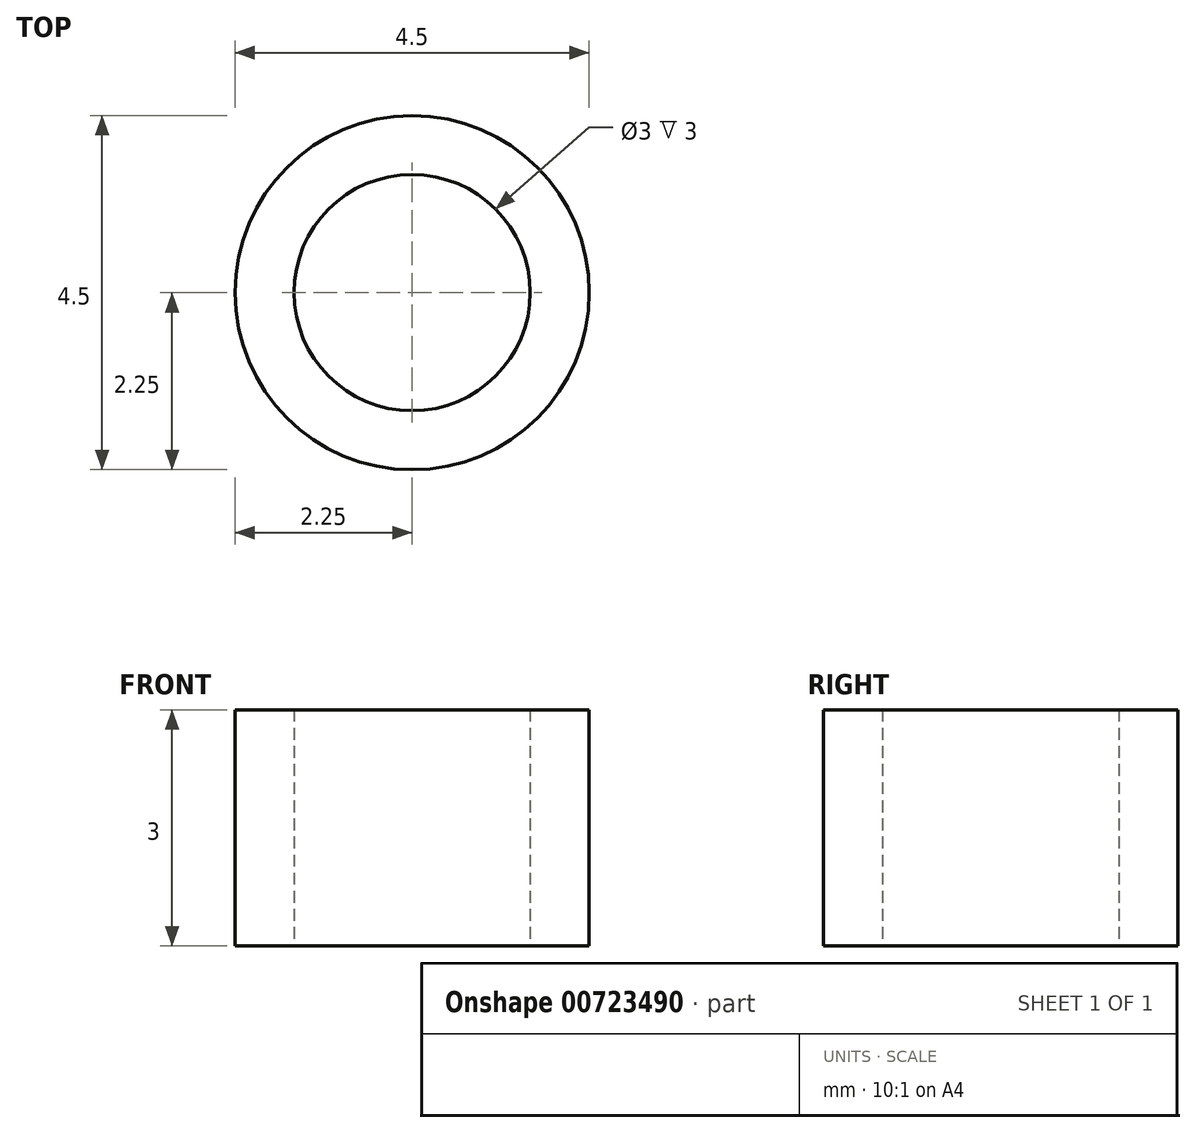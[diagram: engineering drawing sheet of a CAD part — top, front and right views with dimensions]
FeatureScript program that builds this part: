
annotation { "Feature Type Name" : "Feature", "Feature Type Description" : "" }
export const myFeature = defineFeature(function(context is Context, id is Id, definition is map)
    precondition{}
    {
        {
            var Q0;
            Q0=qCreatedBy(makeId("Top.planeOp"),FACE);
            var sketch = newSketch(context, id + "F0", { "sketchPlane" : qUnion([Q0])});
            skCircle(sketch, "E0", {"center": v(0, 0) * mm, "radius": 1.5 * mm});
            skCircle(sketch, "E1", {"center": v(0, 0) * mm, "radius": 2.25 * mm});
            skSolve(sketch);
        }
        {
            var Q0;
            Q0 = qSketchRegion(id + "F0", true);
            extrude(context, id + "F1", {"entities" : qUnion([Q0]), "depth" : 3 * mm, "offsetDistance" : 25 * mm});
        }
    });
